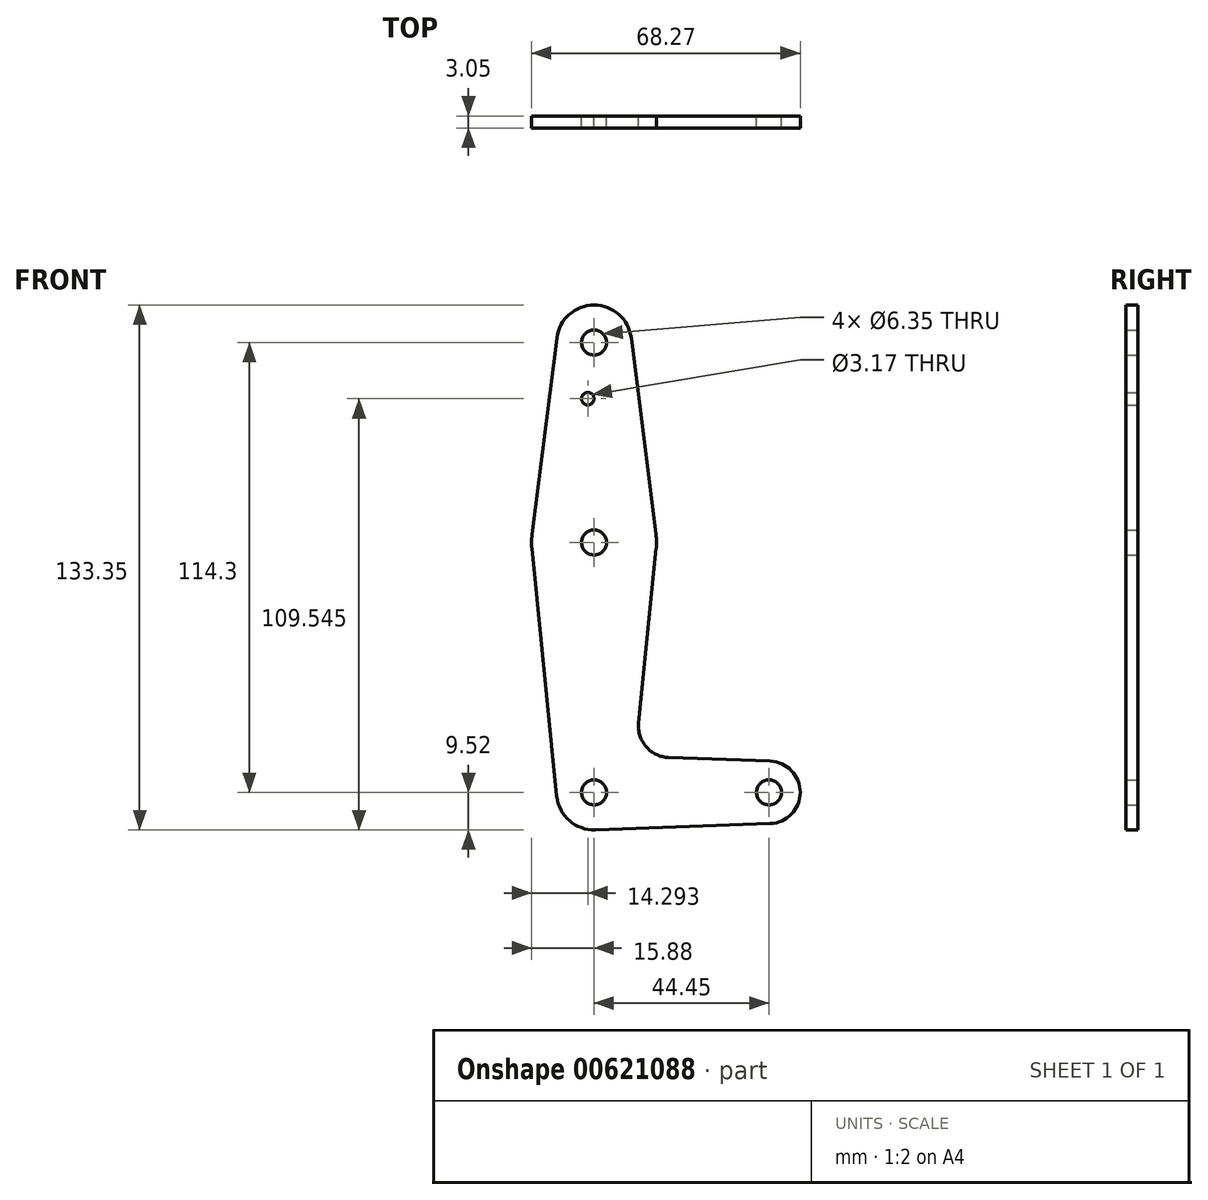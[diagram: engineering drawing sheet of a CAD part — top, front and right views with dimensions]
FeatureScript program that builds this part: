
annotation { "Feature Type Name" : "Feature", "Feature Type Description" : "" }
export const myFeature = defineFeature(function(context is Context, id is Id, definition is map)
    precondition{}
    {
        {
            var Q0;
            Q0=qCreatedBy(makeId("Front.planeOp"),FACE);
            var sketch = newSketch(context, id + "F0", { "sketchPlane" : qUnion([Q0])});
            skLineSegment(sketch, "E0", {"start": v(44.45, 0) * mm, "end": v(0, 0) * mm, "construction": true});
            skCircle(sketch, "E1", {"center": v(0, 114.3) * mm, "radius": 9.53 * mm});
            skCircle(sketch, "E2", {"center": v(0, 63.5) * mm, "radius": 15.88 * mm});
            skCircle(sketch, "E3", {"center": v(0, 0) * mm, "radius": 9.52 * mm});
            skCircle(sketch, "E4", {"center": v(44.45, 0) * mm, "radius": 7.94 * mm});
            skLineSegment(sketch, "E5", {"start": v(0, 63.5) * mm, "end": v(0, 0) * mm, "construction": true});
            skLineSegment(sketch, "E6", {"start": v(0, 114.3) * mm, "end": v(0, 0) * mm, "construction": true});
            skLineSegment(sketch, "E7", {"start": v(-9.45, 115.5) * mm, "end": v(-15.75, 65.48) * mm});
            skLineSegment(sketch, "E8", {"start": v(9.45, 115.5) * mm, "end": v(15.75, 65.48) * mm});
            skLineSegment(sketch, "E9", {"start": v(15.8, 61.91) * mm, "end": v(11.34, 17.59) * mm});
            skLineSegment(sketch, "E10", {"start": v(-15.8, 61.91) * mm, "end": v(-9.48, -0.95) * mm});
            skLineSegment(sketch, "E11", {"start": v(0.34, -9.52) * mm, "end": v(44.73, -7.93) * mm});
            skLineSegment(sketch, "E12", {"start": v(18.97, 8.85) * mm, "end": v(44.73, 7.93) * mm});
            skPoint(sketch, "E13.newPointA", {"position": v(0, 9.53) * mm});
            skArc(sketch, "E13.filletArc", {"start": v(11.34, 17.59) * mm, "mid": v(13.26, 11.57) * mm, "end": v(18.97, 8.85) * mm});
            skCircle(sketch, "E14", {"center": v(-1.59, 100.03) * mm, "radius": 1.59 * mm});
            skCircle(sketch, "E15", {"center": v(0, 114.3) * mm, "radius": 3.18 * mm});
            skCircle(sketch, "E16", {"center": v(0, 63.5) * mm, "radius": 3.18 * mm});
            skCircle(sketch, "E17", {"center": v(0, 0) * mm, "radius": 3.18 * mm});
            skCircle(sketch, "E18", {"center": v(44.45, 0) * mm, "radius": 3.18 * mm});
            skSolve(sketch);
        }
        {
            var Q0;
            Q0 = qSketchRegion(id + "F0", true);
            extrude(context, id + "F1", {"entities" : qUnion([Q0]), "depth" : 3.05 * mm, "offsetDistance" : 25.4 * mm});
        }
    });
